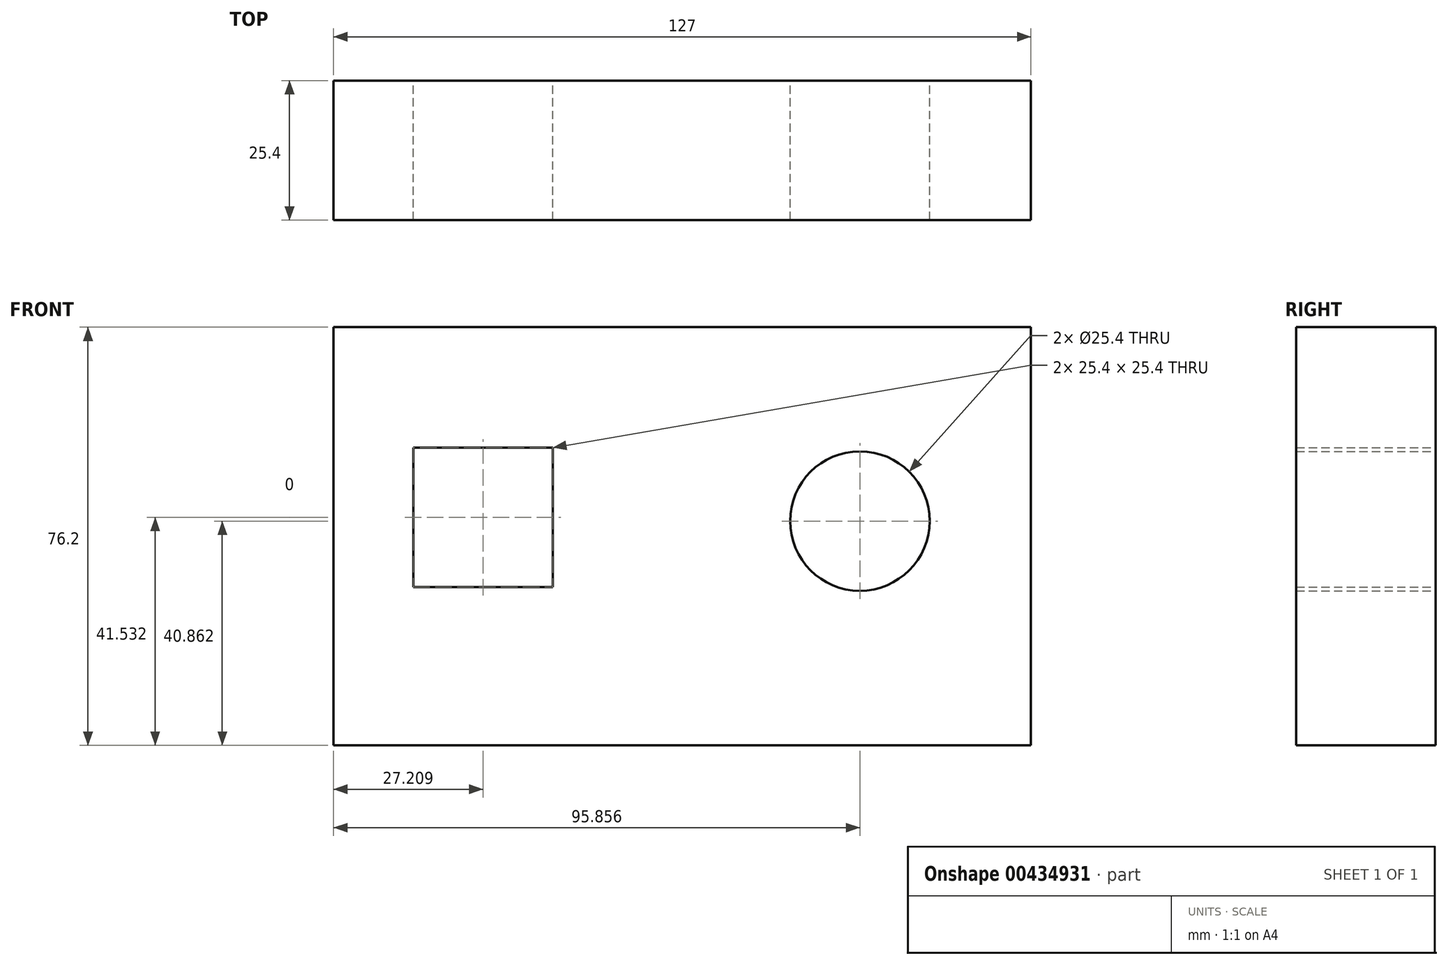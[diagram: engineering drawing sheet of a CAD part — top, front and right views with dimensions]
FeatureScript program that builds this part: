
annotation { "Feature Type Name" : "Feature", "Feature Type Description" : "" }
export const myFeature = defineFeature(function(context is Context, id is Id, definition is map)
    precondition{}
    {
        {
            var Q0;
            Q0=qCreatedBy(makeId("Front.planeOp"),FACE);
            var sketch = newSketch(context, id + "F0", { "sketchPlane" : qUnion([Q0])});
            skLineSegment(sketch, "E0.bottom", {"start": v(-62.63, -6.5) * mm, "end": v(64.37, -6.5) * mm});
            skLineSegment(sketch, "E0.top", {"start": v(-62.63, 69.7) * mm, "end": v(64.37, 69.7) * mm});
            skLineSegment(sketch, "E0.left", {"start": v(-62.63, -6.5) * mm, "end": v(-62.63, 69.7) * mm});
            skLineSegment(sketch, "E0.right", {"start": v(64.37, -6.5) * mm, "end": v(64.37, 69.7) * mm});
            skLineSegment(sketch, "E1.bottom", {"start": v(-48.12, 22.34) * mm, "end": v(-22.72, 22.34) * mm});
            skLineSegment(sketch, "E1.top", {"start": v(-48.12, 47.74) * mm, "end": v(-22.72, 47.74) * mm});
            skLineSegment(sketch, "E1.left", {"start": v(-48.12, 22.34) * mm, "end": v(-48.12, 47.74) * mm});
            skLineSegment(sketch, "E1.right", {"start": v(-22.72, 22.34) * mm, "end": v(-22.72, 47.74) * mm});
            skCircle(sketch, "E2", {"center": v(33.23, 34.37) * mm, "radius": 12.7 * mm});
            skSolve(sketch);
        }
        {
            var Q0;
            Q0=makeQuery(id+"F0.imprint","IMPRINT",FACE,{"disambiguationData":[TD([[makeQuery(id+"F0.imprint","IMPRINT",EDGE,{"derivedFrom":sQuery(id+"F0.wireOp",EDGE,"E0.bottom")}),1.0]])]});
            extrude(context, id + "F1", {"entities" : qUnion([Q0]), "depth" : 25.4 * mm});
        }
    });
